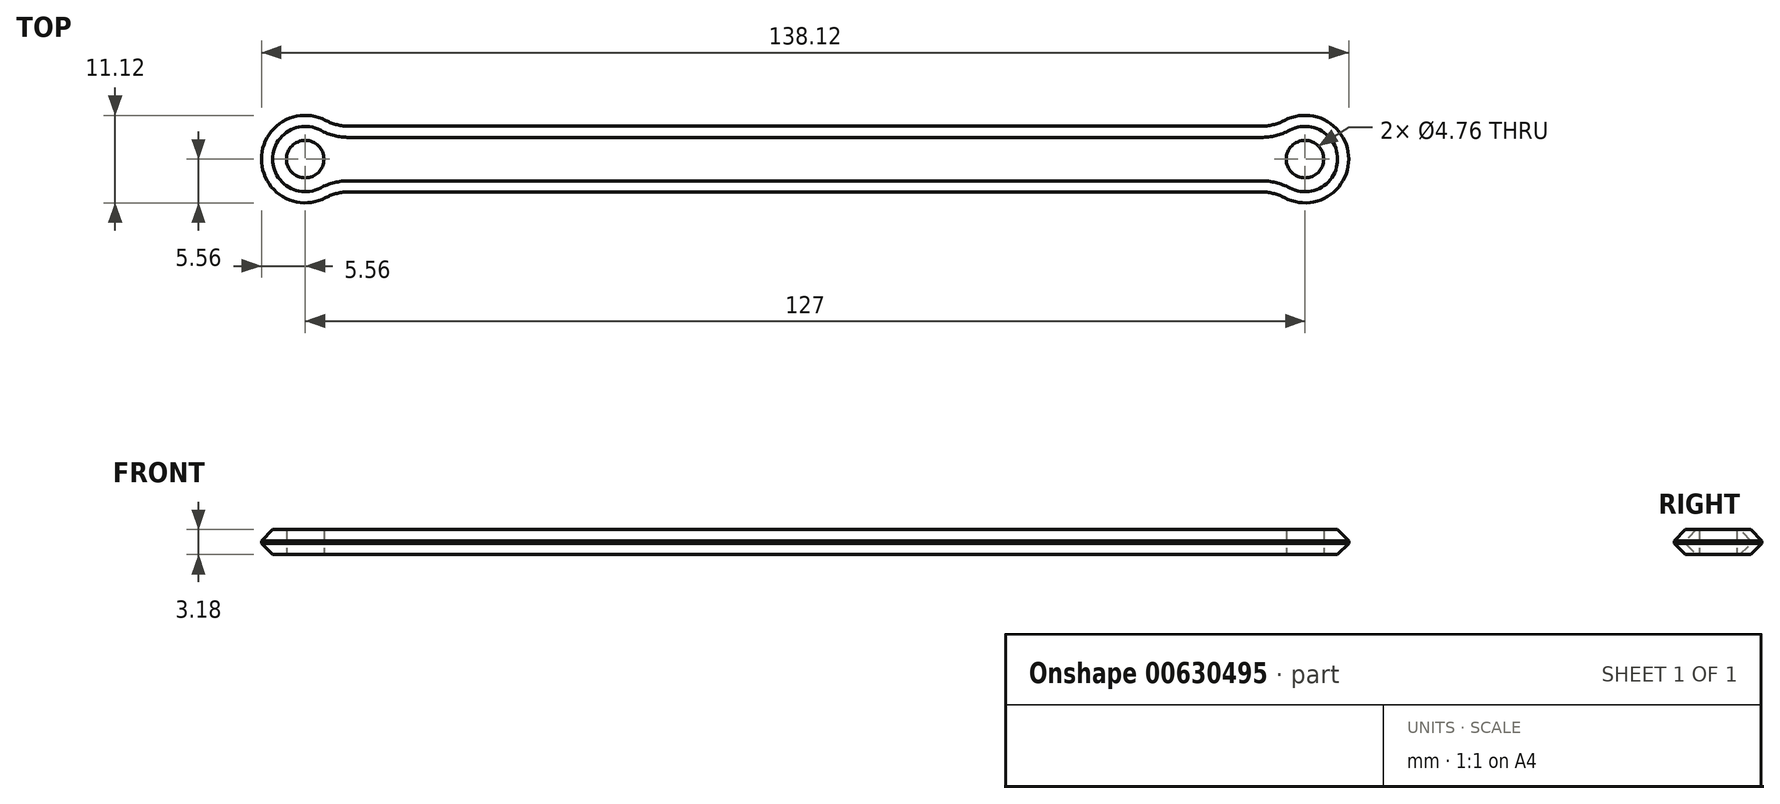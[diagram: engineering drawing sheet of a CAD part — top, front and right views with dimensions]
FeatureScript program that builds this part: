
annotation { "Feature Type Name" : "Feature", "Feature Type Description" : "" }
export const myFeature = defineFeature(function(context is Context, id is Id, definition is map)
    precondition{}
    {
        {
            var Q0;
            Q0=qCreatedBy(makeId("Top.planeOp"),FACE);
            var sketch = newSketch(context, id + "F0", { "sketchPlane" : qUnion([Q0])});
            skCircle(sketch, "E0", {"center": v(0, 0) * mm, "radius": 2.38 * mm});
            skCircle(sketch, "E1", {"center": v(127, 0) * mm, "radius": 2.38 * mm});
            skLineSegment(sketch, "E2", {"start": v(0, 0) * mm, "end": v(127, 0) * mm, "construction": true});
            skArc(sketch, "E3.0", {"start": v(3.68, 4.17) * mm, "mid": v(-5.56, 0) * mm, "end": v(3.68, -4.17) * mm});
            skArc(sketch, "E4.0", {"start": v(123.32, -4.17) * mm, "mid": v(132.56, 0) * mm, "end": v(123.32, 4.17) * mm});
            skLineSegment(sketch, "E5.0.left", {"start": v(3.68, 4.17) * mm, "end": v(123.32, 4.17) * mm});
            skLineSegment(sketch, "E5.0.right", {"start": v(3.68, -4.17) * mm, "end": v(123.32, -4.17) * mm});
            skSolve(sketch);
        }
        {
            var Q0;
            Q0=makeQuery(id+"F0.imprint","IMPRINT",FACE,{"disambiguationData":[TD([[makeQuery(id+"F0.imprint","IMPRINT",EDGE,{"derivedFrom":sQuery(id+"F0.wireOp",EDGE,"E0")}),-1.0]])]});
            extrude(context, id + "F1", {"entities" : qUnion([Q0]), "depth" : 3.17 * mm, "offsetDistance" : 25.4 * mm});
        }
        {
            var Q0;
            Q0=makeQuery(id+"F1.opExtrude","SWEPT_EDGE",EDGE,{"disambiguationData":[OSD([sQuery(id+"F0.wireOp",EDGE,"E3.0"),sQuery(id+"F0.wireOp",EDGE,"E5.0.left")])]});
            var Q1;
            Q1=makeQuery(id+"F1.opExtrude","SWEPT_EDGE",EDGE,{"disambiguationData":[OSD([sQuery(id+"F0.wireOp",EDGE,"E3.0"),sQuery(id+"F0.wireOp",EDGE,"E5.0.right")])]});
            var Q2;
            Q2=makeQuery(id+"F1.opExtrude","SWEPT_EDGE",EDGE,{"disambiguationData":[OSD([sQuery(id+"F0.wireOp",EDGE,"E4.0"),sQuery(id+"F0.wireOp",EDGE,"E5.0.right")])]});
            var Q3;
            Q3=makeQuery(id+"F1.opExtrude","SWEPT_EDGE",EDGE,{"disambiguationData":[OSD([sQuery(id+"F0.wireOp",EDGE,"E4.0"),sQuery(id+"F0.wireOp",EDGE,"E5.0.left")])]});
            fillet(context, id + "F2", {"entities" : qUnion([Q0, Q1, Q2, Q3]), "radius" : 6.35 * mm, "tangentPropagation" : true, "allowEdgeOverflow" : false});
        }
        {
            var Q0;
            Q0=makeQuery(id+"F1.opExtrude","CAP_EDGE",EDGE,{"disambiguationData":[OSD([sQuery(id+"F0.wireOp",EDGE,"E5.0.left")])],"isStart":false});
            var Q1;
            Q1=makeQuery(id+"F1.opExtrude","CAP_EDGE",EDGE,{"disambiguationData":[OSD([sQuery(id+"F0.wireOp",EDGE,"E5.0.left")])],"isStart":true});
            chamfer(context, id + "F3", {"entities" : qUnion([Q0, Q1]), "width" : 1.41 * mm, "tangentPropagation" : true});
        }
    });
